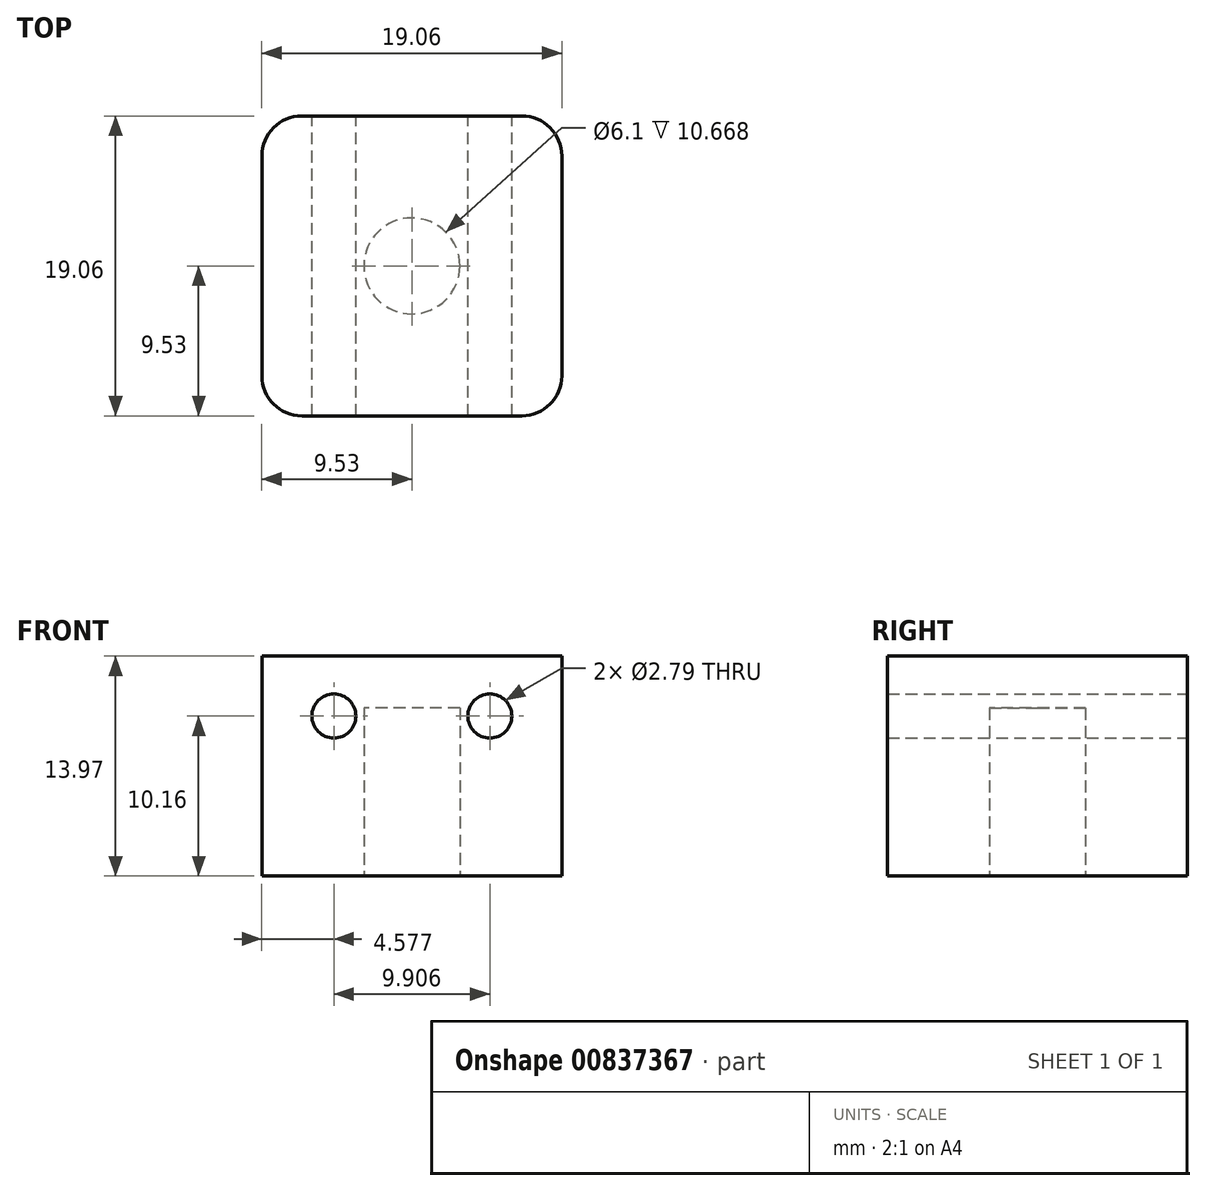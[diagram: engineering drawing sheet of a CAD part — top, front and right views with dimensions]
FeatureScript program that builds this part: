
annotation { "Feature Type Name" : "Feature", "Feature Type Description" : "" }
export const myFeature = defineFeature(function(context is Context, id is Id, definition is map)
    precondition{}
    {
        {
            var Q0;
            Q0=qCreatedBy(makeId("Top.planeOp"),FACE);
            var sketch = newSketch(context, id + "F0", { "sketchPlane" : qUnion([Q0])});
            skCircle(sketch, "E0", {"center": v(0, 0) * mm, "radius": 3.05 * mm});
            skLineSegment(sketch, "E1.bottom", {"start": v(-9.53, 9.53) * mm, "end": v(9.53, 9.53) * mm});
            skLineSegment(sketch, "E1.top", {"start": v(-9.53, -9.52) * mm, "end": v(9.53, -9.52) * mm});
            skLineSegment(sketch, "E1.left", {"start": v(-9.53, 9.53) * mm, "end": v(-9.53, -9.53) * mm});
            skLineSegment(sketch, "E1.right", {"start": v(9.53, 9.53) * mm, "end": v(9.53, -9.53) * mm});
            skLineSegment(sketch, "E2", {"start": v(-9.53, 6.22) * mm, "end": v(9.53, 6.22) * mm});
            skSolve(sketch);
        }
        {
            var Q0;
            Q0=makeQuery(id+"F0.imprint","IMPRINT",FACE,{"disambiguationData":[TD([[makeQuery(id+"F0.imprint","IMPRINT",EDGE,{"derivedFrom":sQuery(id+"F0.wireOp",EDGE,"E0")}),-1.0]])]});
            var Q1;
            {var subQ0=sQuery(id+"F0.wireOp",EDGE,"E1.bottom");Q1=makeQuery(id+"F0.imprint","IMPRINT",FACE,{"disambiguationData":[TD([[makeQuery(id+"F0.imprint","IMPRINT",EDGE,{"derivedFrom":subQ0}),-1.0]])]});}
            extrude(context, id + "F1", {"entities" : qUnion([Q0, Q1]), "depth" : 13.97 * mm, "offsetDistance" : 25.4 * mm});
        }
        {
            var Q0;
            Q0=makeQuery(id+"F1.opExtrude","SWEPT_EDGE",EDGE,{"disambiguationData":[OSD([sQuery(id+"F0.wireOp",EDGE,"E1.bottom"),sQuery(id+"F0.wireOp",EDGE,"E1.right")])]});
            var Q1;
            Q1=makeQuery(id+"F1.opExtrude","SWEPT_EDGE",EDGE,{"disambiguationData":[OSD([sQuery(id+"F0.wireOp",EDGE,"E1.bottom"),sQuery(id+"F0.wireOp",EDGE,"E1.left")])]});
            var Q2;
            Q2=makeQuery(id+"F1.opExtrude","SWEPT_EDGE",EDGE,{"disambiguationData":[OSD([sQuery(id+"F0.wireOp",EDGE,"E1.top"),sQuery(id+"F0.wireOp",EDGE,"E1.left")])]});
            var Q3;
            Q3=makeQuery(id+"F1.opExtrude","SWEPT_EDGE",EDGE,{"disambiguationData":[OSD([sQuery(id+"F0.wireOp",EDGE,"E1.top"),sQuery(id+"F0.wireOp",EDGE,"E1.right")])]});
            fillet(context, id + "F2", {"entities" : qUnion([Q0, Q1, Q2, Q3]), "radius" : 2.54 * mm, "tangentPropagation" : true, "allowEdgeOverflow" : false});
        }
        {
            var Q0;
            Q0=makeQuery(id+"F1.opExtrude","SWEPT_FACE",FACE,{"disambiguationData":[OSD([sQuery(id+"F0.wireOp",EDGE,"E1.bottom")])]});
            var sketch = newSketch(context, id + "F3", { "sketchPlane" : qUnion([Q0])});
            skLineSegment(sketch, "E3", {"start": v(-6.99, 13.97) * mm, "end": v(6.99, 13.97) * mm});
            skLineSegment(sketch, "E4", {"start": v(0, 13.97) * mm, "end": v(0, 6.35) * mm});
            skCircle(sketch, "E5", {"center": v(4.95, 10.16) * mm, "radius": 1.4 * mm});
            skCircle(sketch, "E6.MirrorC", {"center": v(-4.95, 10.16) * mm, "radius": 1.4 * mm});
            skLineSegment(sketch, "E7", {"start": v(-2.03, 10.16) * mm, "end": v(3.56, 10.16) * mm});
            skSolve(sketch);
        }
        {
            var Q0;
            Q0 = qSketchRegion(id + "F3", true);
            extrude(context, id + "F4", {"entities" : qUnion([Q0]), "operationType" : NewBodyOperationType.REMOVE, "oppositeDirection" : true, "depth" : 25.4 * mm, "offsetDistance" : 25.4 * mm});
        }
        {
            var Q0;
            Q0=makeQuery(id+"F1.opExtrude","CAP_FACE",FACE,{"disambiguationData":[OSD([sQuery(id+"F0.wireOp",EDGE,"E0"),sQuery(id+"F0.wireOp",EDGE,"E1.bottom"),sQuery(id+"F0.wireOp",EDGE,"E1.top"),sQuery(id+"F0.wireOp",EDGE,"E1.left"),sQuery(id+"F0.wireOp",EDGE,"E1.right")])],"isStart":false});
            var sketch = newSketch(context, id + "F5", { "sketchPlane" : qUnion([Q0])});
            skCircle(sketch, "E8", {"center": v(0, 0) * mm, "radius": 3.05 * mm});
            skSolve(sketch);
        }
        {
            var Q0;
            Q0 = qSketchRegion(id + "F5", true);
            extrude(context, id + "F6", {"entities" : qUnion([Q0]), "operationType" : NewBodyOperationType.ADD, "oppositeDirection" : true, "depth" : 3.3 * mm, "offsetDistance" : 25.4 * mm});
        }
    });
